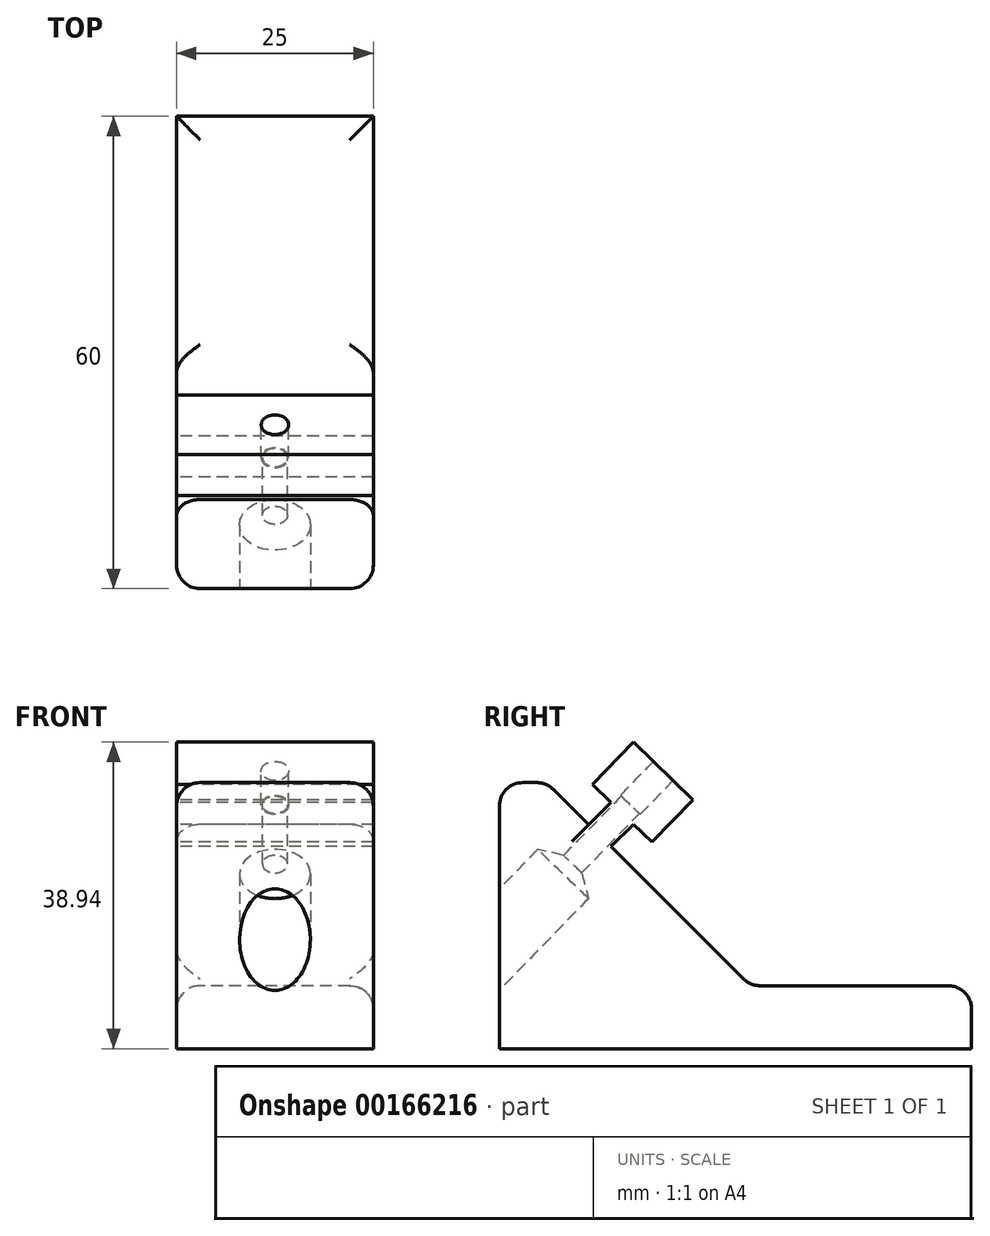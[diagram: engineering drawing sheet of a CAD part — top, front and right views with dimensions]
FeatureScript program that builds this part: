
annotation { "Feature Type Name" : "Feature", "Feature Type Description" : "" }
export const myFeature = defineFeature(function(context is Context, id is Id, definition is map)
    precondition{}
    {
        {
            var Q0;
            Q0=qCreatedBy(makeId("Right.planeOp"),FACE);
            var sketch = newSketch(context, id + "F0", { "sketchPlane" : qUnion([Q0])});
            skLineSegment(sketch, "E0", {"start": v(0, 0) * mm, "end": v(60, 0) * mm});
            skLineSegment(sketch, "E1", {"start": v(60, 0) * mm, "end": v(60, 8) * mm});
            skLineSegment(sketch, "E2", {"start": v(60, 8) * mm, "end": v(31.88, 8) * mm});
            skLineSegment(sketch, "E3", {"start": v(11.33, 28.47) * mm, "end": v(14.16, 31.3) * mm});
            skLineSegment(sketch, "E4", {"start": v(19.36, 26.24) * mm, "end": v(24.59, 31.62) * mm});
            skLineSegment(sketch, "E5", {"start": v(24.59, 31.62) * mm, "end": v(17.06, 38.94) * mm});
            skLineSegment(sketch, "E6", {"start": v(17.06, 38.94) * mm, "end": v(11.83, 33.56) * mm});
            skLineSegment(sketch, "E7", {"start": v(17.03, 28.5) * mm, "end": v(14.2, 25.68) * mm});
            skLineSegment(sketch, "E8", {"start": v(6, 33.8) * mm, "end": v(0, 33.8) * mm});
            skLineSegment(sketch, "E9", {"start": v(0, 33.8) * mm, "end": v(0, 0) * mm});
            skLineSegment(sketch, "E10", {"start": v(14.16, 31.3) * mm, "end": v(11.83, 33.56) * mm});
            skLineSegment(sketch, "E11", {"start": v(17.03, 28.5) * mm, "end": v(19.36, 26.24) * mm});
            skLineSegment(sketch, "E12", {"start": v(31.88, 8) * mm, "end": v(14.2, 25.68) * mm});
            skLineSegment(sketch, "E13", {"start": v(6, 33.8) * mm, "end": v(11.33, 28.47) * mm});
            skSolve(sketch);
        }
        {
            var Q0;
            Q0=makeQuery(id+"F0.imprint","IMPRINT",FACE,{"disambiguationData":[TD([[makeQuery(id+"F0.imprint","IMPRINT",EDGE,{"derivedFrom":sQuery(id+"F0.wireOp",EDGE,"E0")}),1.0]])]});
            extrude(context, id + "F1", {"entities" : qUnion([Q0]), "depth" : 25 * mm});
        }
        {
            var Q0;
            Q0=makeQuery(id+"F1.opExtrude","SWEPT_FACE",FACE,{"disambiguationData":[OSD([sQuery(id+"F0.wireOp",EDGE,"E2")])]});
            var Q1;
            Q1=makeQuery(id+"F1.opExtrude","CAP_EDGE",EDGE,{"disambiguationData":[OSD([sQuery(id+"F0.wireOp",EDGE,"oUCWIk0d-s3rL-LjrQ-Pm3v-g5gD6WH3k69Y")])],"isStart":false});
            var Q2;
            Q2=makeQuery(id+"F1.opExtrude","CAP_EDGE",EDGE,{"disambiguationData":[OSD([sQuery(id+"F0.wireOp",EDGE,"gGHxSdgf-QsQ2-Vr1K-mVMZ-eMd9LpW39Ww4")])],"isStart":false});
            var Q3;
            Q3=makeQuery(id+"F1.opExtrude","CAP_EDGE",EDGE,{"disambiguationData":[OSD([sQuery(id+"F0.wireOp",EDGE,"c3CVaNKi-cnUc-T3ha-DsAc-fHBxSejp19oV")])],"isStart":false});
            var Q4;
            Q4=makeQuery(id+"F1.opExtrude","CAP_EDGE",EDGE,{"disambiguationData":[OSD([sQuery(id+"F0.wireOp",EDGE,"c3CVaNKi-cnUc-T3ha-DsAc-fHBxSejp19oV")])],"isStart":true});
            var Q5;
            Q5=makeQuery(id+"F1.opExtrude","CAP_EDGE",EDGE,{"disambiguationData":[OSD([sQuery(id+"F0.wireOp",EDGE,"oUCWIk0d-s3rL-LjrQ-Pm3v-g5gD6WH3k69Y")])],"isStart":true});
            var Q6;
            Q6=makeQuery(id+"F1.opExtrude","CAP_EDGE",EDGE,{"disambiguationData":[OSD([sQuery(id+"F0.wireOp",EDGE,"gGHxSdgf-QsQ2-Vr1K-mVMZ-eMd9LpW39Ww4")])],"isStart":true});
            var Q7;
            Q7=makeQuery(id+"F1.opExtrude","SWEPT_FACE",FACE,{"disambiguationData":[OSD([sQuery(id+"F0.wireOp",EDGE,"E8")])]});
            var Q8;
            Q8=makeQuery(id+"F1.opExtrude","CAP_EDGE",EDGE,{"disambiguationData":[OSD([sQuery(id+"F0.wireOp",EDGE,"E13")])],"isStart":false});
            var Q9;
            Q9=makeQuery(id+"F1.opExtrude","CAP_EDGE",EDGE,{"disambiguationData":[OSD([sQuery(id+"F0.wireOp",EDGE,"E9")])],"isStart":false});
            var Q10;
            Q10=makeQuery(id+"F1.opExtrude","CAP_EDGE",EDGE,{"disambiguationData":[OSD([sQuery(id+"F0.wireOp",EDGE,"E9")])],"isStart":true});
            var Q11;
            Q11=makeQuery(id+"F1.opExtrude","CAP_EDGE",EDGE,{"disambiguationData":[OSD([sQuery(id+"F0.wireOp",EDGE,"E13")])],"isStart":true});
            fillet(context, id + "F2", {"entities" : qUnion([Q0, Q1, Q2, Q3, Q4, Q5, Q6, Q7, Q8, Q9, Q10, Q11]), "radius" : 3 * mm, "tangentPropagation" : true, "allowEdgeOverflow" : false});
        }
        {
            var Q0;
            Q0=makeQuery(id+"F1.opExtrude","SWEPT_FACE",FACE,{"disambiguationData":[OSD([sQuery(id+"F0.wireOp",EDGE,"E5")])]});
            var sketch = newSketch(context, id + "F3", { "sketchPlane" : qUnion([Q0])});
            skPoint(sketch, "E14", {"position": v(12.5, -9.66) * mm});
            skPoint(sketch, "E14.positionSnap0", {"position": v(0, -9.66) * mm});
            skPoint(sketch, "E14.positionSnap1", {"position": v(12.5, -14.9) * mm});
            skSolve(sketch);
        }
        {
            var Q0;
            Q0=sQuery(id+"F3.wireOp",VERTEX,"E14");
            var Q1;
            Q1=makeQuery(id+"F1.opExtrude","SWEPT_BODY",BODY,{"disambiguationData":[OSD([sQuery(id+"F0.wireOp",EDGE,"E0"),sQuery(id+"F0.wireOp",EDGE,"E1"),sQuery(id+"F0.wireOp",EDGE,"E2"),sQuery(id+"F0.wireOp",EDGE,"E3"),sQuery(id+"F0.wireOp",EDGE,"E4"),sQuery(id+"F0.wireOp",EDGE,"E5"),sQuery(id+"F0.wireOp",EDGE,"E6"),sQuery(id+"F0.wireOp",EDGE,"E7"),sQuery(id+"F0.wireOp",EDGE,"E8"),sQuery(id+"F0.wireOp",EDGE,"E9"),sQuery(id+"F0.wireOp",EDGE,"E10"),sQuery(id+"F0.wireOp",EDGE,"E11"),sQuery(id+"F0.wireOp",EDGE,"E12"),sQuery(id+"F0.wireOp",EDGE,"E13"),sQuery(id+"F0.wireOp",EDGE,"c3CVaNKi-cnUc-T3ha-DsAc-fHBxSejp19oV"),sQuery(id+"F0.wireOp",EDGE,"oUCWIk0d-s3rL-LjrQ-Pm3v-g5gD6WH3k69Y"),sQuery(id+"F0.wireOp",EDGE,"gGHxSdgf-QsQ2-Vr1K-mVMZ-eMd9LpW39Ww4")])]});
            hole(context, id + "F4", {"style" : HoleStyle.C_BORE, "endStyle" : HoleEndStyle.THROUGH, "holeDiameter" : 3.2 * mm, "cBoreDiameter" : 3.5 * mm, "cBoreDepth" : 6 * mm, "locations" : qUnion([Q0]), "scope" : qUnion([Q1]), "isTappedThrough" : true});
        }
        {
            var Q0;
            Q0=makeQuery(id+"F1.opExtrude","SWEPT_FACE",FACE,{"disambiguationData":[OSD([sQuery(id+"F0.wireOp",EDGE,"E5")])]});
            cPlane(context, id + "F5", {"entities" : qUnion([Q0]), "cplaneType" : CPlaneType.OFFSET, "offset" : 35 * mm, "oppositeDirection" : true, "width" : 150 * mm, "height" : 150 * mm});
        }
        {
            var Q0;
            Q0=qCreatedBy(id+"F5.planeOp",FACE);
            var sketch = newSketch(context, id + "F6", { "sketchPlane" : qUnion([Q0])});
            skPoint(sketch, "E15.0", {"position": v(12.5, -9.66) * mm});
            skSolve(sketch);
        }
        {
            var Q0;
            Q0=sQuery(id+"F6.wireOp",VERTEX,"E15.0");
            var Q1;
            Q1=makeQuery(id+"F1.opExtrude","SWEPT_BODY",BODY,{"disambiguationData":[OSD([sQuery(id+"F0.wireOp",EDGE,"E0"),sQuery(id+"F0.wireOp",EDGE,"E1"),sQuery(id+"F0.wireOp",EDGE,"E2"),sQuery(id+"F0.wireOp",EDGE,"E3"),sQuery(id+"F0.wireOp",EDGE,"E4"),sQuery(id+"F0.wireOp",EDGE,"E5"),sQuery(id+"F0.wireOp",EDGE,"E6"),sQuery(id+"F0.wireOp",EDGE,"E7"),sQuery(id+"F0.wireOp",EDGE,"E8"),sQuery(id+"F0.wireOp",EDGE,"E9"),sQuery(id+"F0.wireOp",EDGE,"E10"),sQuery(id+"F0.wireOp",EDGE,"E11"),sQuery(id+"F0.wireOp",EDGE,"E12"),sQuery(id+"F0.wireOp",EDGE,"E13")])]});
            hole(context, id + "F7", {"style" : HoleStyle.SIMPLE, "endStyle" : HoleEndStyle.BLIND, "oppositeDirection" : true, "holeDiameter" : 9 * mm, "holeDepth" : 7 * mm, "locations" : qUnion([Q0]), "scope" : qUnion([Q1])});
        }
    });
